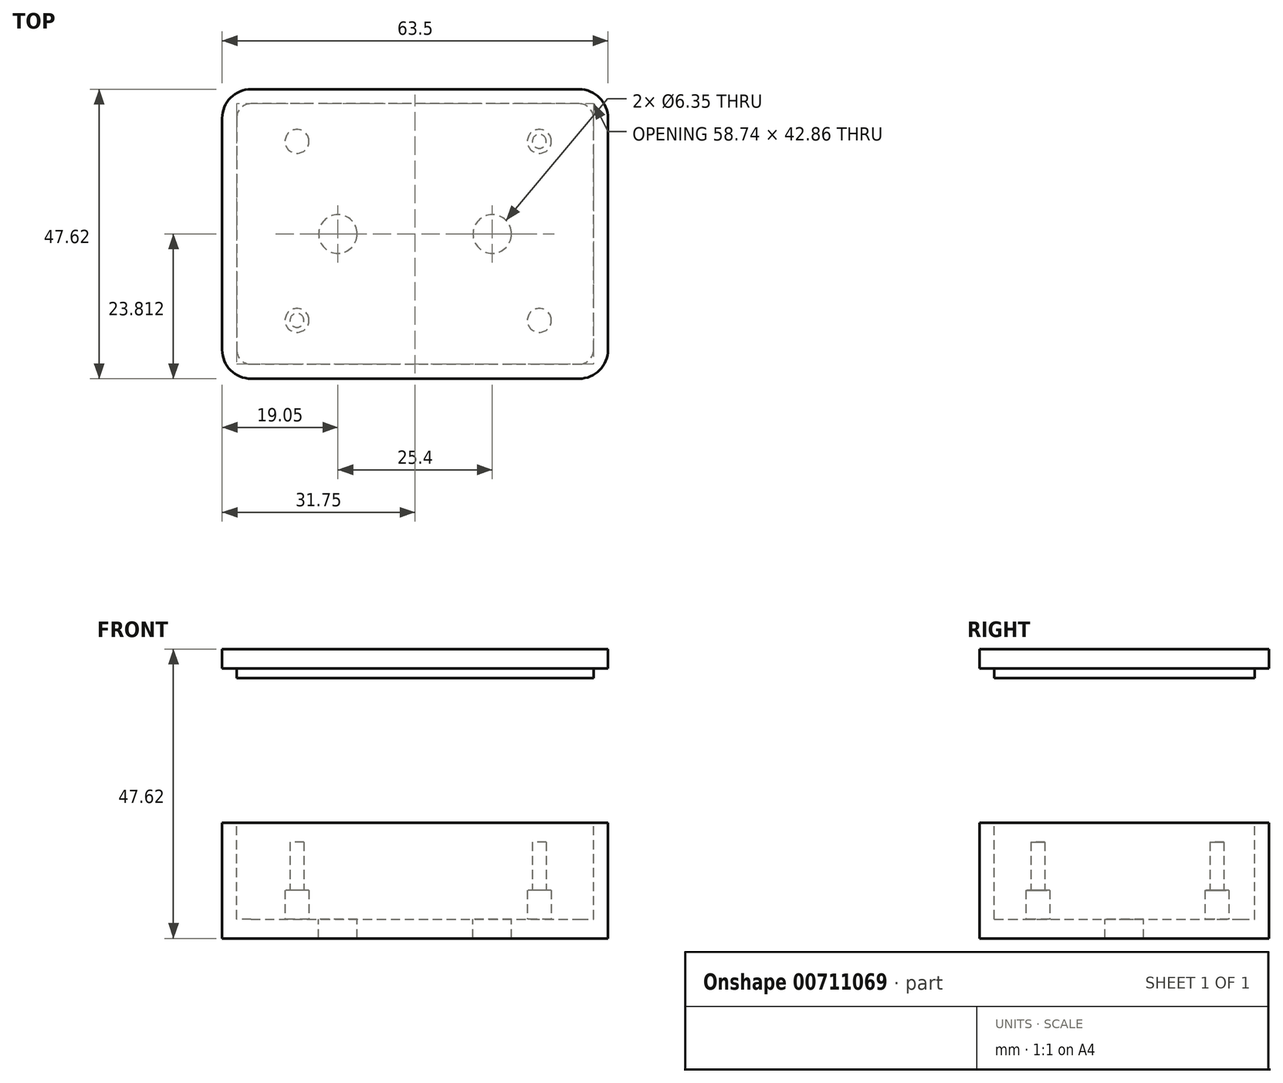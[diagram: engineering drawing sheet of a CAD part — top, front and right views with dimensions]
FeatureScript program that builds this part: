
annotation { "Feature Type Name" : "Feature", "Feature Type Description" : "" }
export const myFeature = defineFeature(function(context is Context, id is Id, definition is map)
    precondition{}
    {
        {
            var Q0;
            Q0=qCreatedBy(makeId("Top.planeOp"),FACE);
            var sketch = newSketch(context, id + "F0", { "sketchPlane" : qUnion([Q0])});
            skLineSegment(sketch, "E0.bottom", {"start": v(0, 0) * mm, "end": v(63.5, 0) * mm});
            skLineSegment(sketch, "E0.top", {"start": v(0, 47.62) * mm, "end": v(63.5, 47.62) * mm});
            skLineSegment(sketch, "E0.left", {"start": v(0, 0) * mm, "end": v(0, 47.62) * mm});
            skLineSegment(sketch, "E0.right", {"start": v(63.5, 0) * mm, "end": v(63.5, 47.62) * mm});
            skSolve(sketch);
        }
        {
            var Q0;
            Q0=makeQuery(id+"F0.imprint","IMPRINT",FACE,{"disambiguationData":[TD([[makeQuery(id+"F0.imprint","IMPRINT",EDGE,{"derivedFrom":sQuery(id+"F0.wireOp",EDGE,"E0.bottom")}),1.0]])]});
            extrude(context, id + "F1", {"entities" : qUnion([Q0]), "depth" : 19.05 * mm, "offsetDistance" : 25.4 * mm});
        }
        {
            var Q0;
            Q0=makeQuery(id+"F1.opExtrude","SWEPT_EDGE",EDGE,{"disambiguationData":[OSD([sQuery(id+"F0.wireOp",EDGE,"E0.bottom"),sQuery(id+"F0.wireOp",EDGE,"E0.left")])]});
            var Q1;
            Q1=makeQuery(id+"F1.opExtrude","SWEPT_EDGE",EDGE,{"disambiguationData":[OSD([sQuery(id+"F0.wireOp",EDGE,"E0.bottom"),sQuery(id+"F0.wireOp",EDGE,"E0.right")])]});
            var Q2;
            Q2=makeQuery(id+"F1.opExtrude","SWEPT_EDGE",EDGE,{"disambiguationData":[OSD([sQuery(id+"F0.wireOp",EDGE,"E0.top"),sQuery(id+"F0.wireOp",EDGE,"E0.right")])]});
            var Q3;
            Q3=makeQuery(id+"F1.opExtrude","SWEPT_EDGE",EDGE,{"disambiguationData":[OSD([sQuery(id+"F0.wireOp",EDGE,"E0.top"),sQuery(id+"F0.wireOp",EDGE,"E0.left")])]});
            fillet(context, id + "F2", {"entities" : qUnion([Q0, Q1, Q2, Q3]), "radius" : 4.76 * mm, "tangentPropagation" : true, "allowEdgeOverflow" : false});
        }
        {
            var Q0;
            Q0=makeQuery(id+"F1.opExtrude","CAP_FACE",FACE,{"disambiguationData":[OSD([sQuery(id+"F0.wireOp",EDGE,"E0.bottom"),sQuery(id+"F0.wireOp",EDGE,"E0.top"),sQuery(id+"F0.wireOp",EDGE,"E0.left"),sQuery(id+"F0.wireOp",EDGE,"E0.right")])],"isStart":false});
            var sketch = newSketch(context, id + "F3", { "sketchPlane" : qUnion([Q0])});
            skLineSegment(sketch, "E1.0", {"start": v(58.74, 45.24) * mm, "end": v(4.76, 45.24) * mm});
            skLineSegment(sketch, "E1.1", {"start": v(61.12, 4.76) * mm, "end": v(61.12, 42.86) * mm});
            skLineSegment(sketch, "E1.2", {"start": v(4.76, 2.38) * mm, "end": v(58.74, 2.38) * mm});
            skLineSegment(sketch, "E1.3", {"start": v(2.38, 42.86) * mm, "end": v(2.38, 4.76) * mm});
            skPoint(sketch, "E2.visualSharp", {"position": v(61.12, 45.24) * mm});
            skArc(sketch, "E2.filletArc", {"start": v(61.12, 42.86) * mm, "mid": v(60.42, 44.55) * mm, "end": v(58.74, 45.24) * mm});
            skPoint(sketch, "E3.visualSharp", {"position": v(61.12, 2.38) * mm});
            skArc(sketch, "E3.filletArc", {"start": v(58.74, 2.38) * mm, "mid": v(60.42, 3.08) * mm, "end": v(61.12, 4.76) * mm});
            skPoint(sketch, "E4.visualSharp", {"position": v(2.38, 2.38) * mm});
            skArc(sketch, "E4.filletArc", {"start": v(2.38, 4.76) * mm, "mid": v(3.08, 3.08) * mm, "end": v(4.76, 2.38) * mm});
            skPoint(sketch, "E5.visualSharp", {"position": v(2.38, 45.24) * mm});
            skArc(sketch, "E5.filletArc", {"start": v(4.76, 45.24) * mm, "mid": v(3.08, 44.55) * mm, "end": v(2.38, 42.86) * mm});
            skSolve(sketch);
        }
        {
            var Q0;
            Q0 = qSketchRegion(id + "F3", true);
            var Q1;
            Q1=sQuery(id+"F3.wireOp",EDGE,"E1.1");
            extrude(context, id + "F4", {"entities" : qUnion([Q0]), "operationType" : NewBodyOperationType.REMOVE, "surfaceEntities" : qUnion([Q1]), "oppositeDirection" : true, "depth" : 15.88 * mm, "offsetDistance" : 25.4 * mm});
        }
        {
            var Q0;
            Q0=makeQuery(id+"F4.boolean.opBoolean","COPY",FACE,{"derivedFrom":makeQuery(id+"F4.opExtrude","CAP_FACE",FACE,{"disambiguationData":[OSD([sQuery(id+"F3.wireOp",EDGE,"E1.0"),sQuery(id+"F3.wireOp",EDGE,"E1.1"),sQuery(id+"F3.wireOp",EDGE,"E1.2"),sQuery(id+"F3.wireOp",EDGE,"E1.3"),sQuery(id+"F3.wireOp",EDGE,"E2.filletArc"),sQuery(id+"F3.wireOp",EDGE,"E3.filletArc"),sQuery(id+"F3.wireOp",EDGE,"E4.filletArc"),sQuery(id+"F3.wireOp",EDGE,"E5.filletArc")])],"isStart":false})});
            var sketch = newSketch(context, id + "F5", { "sketchPlane" : qUnion([Q0])});
            skCircle(sketch, "E6", {"center": v(12.32, 9.59) * mm, "radius": 1.14 * mm});
            skCircle(sketch, "E7", {"center": v(52.2, 39.05) * mm, "radius": 1.14 * mm});
            skLineSegment(sketch, "E8.bottom", {"start": v(55.25, 42.1) * mm, "end": v(8.25, 42.1) * mm, "construction": true});
            skLineSegment(sketch, "E8.top", {"start": v(55.25, 5.52) * mm, "end": v(8.25, 5.52) * mm, "construction": true});
            skLineSegment(sketch, "E8.left", {"start": v(55.25, 42.1) * mm, "end": v(55.25, 5.52) * mm, "construction": true});
            skLineSegment(sketch, "E8.right", {"start": v(8.25, 42.1) * mm, "end": v(8.25, 5.52) * mm, "construction": true});
            skLineSegment(sketch, "E9", {"start": v(31.75, 5.52) * mm, "end": v(31.75, 2.38) * mm, "construction": true});
            skLineSegment(sketch, "E10", {"start": v(55.25, 23.81) * mm, "end": v(61.12, 23.81) * mm, "construction": true});
            skSolve(sketch);
        }
        {
            var Q0;
            Q0 = qSketchRegion(id + "F5", true);
            var Q1;
            Q1=sQuery(id+"F5.wireOp",EDGE,"E6");
            var Q2;
            Q2=makeQuery(id+"F1.opExtrude","CAP_FACE",FACE,{"disambiguationData":[OSD([sQuery(id+"F0.wireOp",EDGE,"E0.bottom"),sQuery(id+"F0.wireOp",EDGE,"E0.top"),sQuery(id+"F0.wireOp",EDGE,"E0.left"),sQuery(id+"F0.wireOp",EDGE,"E0.right")])],"isStart":false});
            extrude(context, id + "F6", {"entities" : qUnion([Q0]), "operationType" : NewBodyOperationType.ADD, "surfaceEntities" : qUnion([Q1]), "depth" : 12.7 * mm, "endBoundEntityFace" : qUnion([Q2]), "offsetDistance" : 25.4 * mm});
        }
        {
            var Q0;
            Q0=makeQuery(id+"F4.boolean.opBoolean","COPY",FACE,{"derivedFrom":makeQuery(id+"F4.opExtrude","CAP_FACE",FACE,{"disambiguationData":[OSD([sQuery(id+"F3.wireOp",EDGE,"E1.0"),sQuery(id+"F3.wireOp",EDGE,"E1.1"),sQuery(id+"F3.wireOp",EDGE,"E1.2"),sQuery(id+"F3.wireOp",EDGE,"E1.3"),sQuery(id+"F3.wireOp",EDGE,"E2.filletArc"),sQuery(id+"F3.wireOp",EDGE,"E3.filletArc"),sQuery(id+"F3.wireOp",EDGE,"E4.filletArc"),sQuery(id+"F3.wireOp",EDGE,"E5.filletArc")])],"isStart":false})});
            var sketch = newSketch(context, id + "F7", { "sketchPlane" : qUnion([Q0])});
            skCircle(sketch, "E11.0", {"center": v(12.32, 9.59) * mm, "radius": 1.97 * mm});
            skCircle(sketch, "E12.0", {"center": v(52.2, 39.05) * mm, "radius": 1.97 * mm});
            skCircle(sketch, "E13", {"center": v(12.32, 39.05) * mm, "radius": 1.97 * mm});
            skCircle(sketch, "E14", {"center": v(52.2, 9.59) * mm, "radius": 1.97 * mm});
            skSolve(sketch);
        }
        {
            var Q0;
            Q0 = qSketchRegion(id + "F7", true);
            extrude(context, id + "F8", {"entities" : qUnion([Q0]), "operationType" : NewBodyOperationType.ADD, "depth" : 4.76 * mm, "offsetDistance" : 25.4 * mm});
        }
        {
            var Q0;
            Q0=makeQuery(id+"F4.boolean.opBoolean","COPY",FACE,{"derivedFrom":makeQuery(id+"F4.opExtrude","CAP_FACE",FACE,{"disambiguationData":[OSD([sQuery(id+"F3.wireOp",EDGE,"E1.0"),sQuery(id+"F3.wireOp",EDGE,"E1.1"),sQuery(id+"F3.wireOp",EDGE,"E1.2"),sQuery(id+"F3.wireOp",EDGE,"E1.3"),sQuery(id+"F3.wireOp",EDGE,"E2.filletArc"),sQuery(id+"F3.wireOp",EDGE,"E3.filletArc"),sQuery(id+"F3.wireOp",EDGE,"E4.filletArc"),sQuery(id+"F3.wireOp",EDGE,"E5.filletArc")])],"isStart":false})});
            var sketch = newSketch(context, id + "F9", { "sketchPlane" : qUnion([Q0])});
            skCircle(sketch, "E15", {"center": v(44.45, 23.81) * mm, "radius": 3.18 * mm});
            skCircle(sketch, "E16", {"center": v(19.05, 23.81) * mm, "radius": 3.18 * mm});
            skLineSegment(sketch, "E17", {"start": v(44.45, 23.81) * mm, "end": v(19.05, 23.81) * mm, "construction": true});
            skLineSegment(sketch, "E18", {"start": v(31.75, 23.81) * mm, "end": v(31.75, 2.38) * mm, "construction": true});
            skLineSegment(sketch, "E19", {"start": v(31.75, 23.81) * mm, "end": v(31.75, 45.24) * mm, "construction": true});
            skSolve(sketch);
        }
        {
            var Q0;
            Q0 = qSketchRegion(id + "F9", true);
            extrude(context, id + "F10", {"entities" : qUnion([Q0]), "operationType" : NewBodyOperationType.REMOVE, "oppositeDirection" : true, "depth" : 25.4 * mm, "offsetDistance" : 25.4 * mm});
        }
        {
            var Q0;
            Q0=makeQuery(id+"F1.opExtrude","CAP_FACE",FACE,{"disambiguationData":[OSD([sQuery(id+"F0.wireOp",EDGE,"E0.bottom"),sQuery(id+"F0.wireOp",EDGE,"E0.top"),sQuery(id+"F0.wireOp",EDGE,"E0.left"),sQuery(id+"F0.wireOp",EDGE,"E0.right")])],"isStart":false});
            cPlane(context, id + "F11", {"entities" : qUnion([Q0]), "cplaneType" : CPlaneType.OFFSET, "offset" : 25.4 * mm, "width" : 152.4 * mm, "height" : 152.4 * mm});
        }
        {
            var Q0;
            Q0=qCreatedBy(id+"F11.planeOp",FACE);
            var sketch = newSketch(context, id + "F12", { "sketchPlane" : qUnion([Q0])});
            skLineSegment(sketch, "E20.0", {"start": v(0, 4.76) * mm, "end": v(0, 42.86) * mm});
            skLineSegment(sketch, "E21.0", {"start": v(4.76, 47.62) * mm, "end": v(58.74, 47.62) * mm});
            skArc(sketch, "E22.0", {"start": v(4.76, 47.62) * mm, "mid": v(1.4, 46.23) * mm, "end": v(0, 42.86) * mm});
            skArc(sketch, "E23.0", {"start": v(63.5, 42.86) * mm, "mid": v(62.1, 46.23) * mm, "end": v(58.74, 47.62) * mm});
            skLineSegment(sketch, "E24.0", {"start": v(63.5, 4.76) * mm, "end": v(63.5, 42.86) * mm});
            skArc(sketch, "E25.0", {"start": v(58.74, 0) * mm, "mid": v(62.1, 1.4) * mm, "end": v(63.5, 4.76) * mm});
            skLineSegment(sketch, "E26.0", {"start": v(4.76, 0) * mm, "end": v(58.74, 0) * mm});
            skArc(sketch, "E27.0", {"start": v(0, 4.76) * mm, "mid": v(1.4, 1.4) * mm, "end": v(4.76, 0) * mm});
            skSolve(sketch);
        }
        {
            var Q0;
            Q0=makeQuery(id+"F12.imprint","IMPRINT",FACE,{"disambiguationData":[TD([[makeQuery(id+"F12.imprint","IMPRINT",EDGE,{"derivedFrom":sQuery(id+"F12.wireOp",EDGE,"E20.0")}),-1.0]])]});
            var Q1;
            Q1=sQuery(id+"F12.wireOp",EDGE,"E20.0");
            extrude(context, id + "F13", {"entities" : qUnion([Q0]), "surfaceEntities" : qUnion([Q1]), "depth" : 3.17 * mm, "offsetDistance" : 25.4 * mm});
        }
        {
            var Q0;
            Q0=makeQuery(id+"F13.opExtrude","CAP_FACE",FACE,{"disambiguationData":[OSD([sQuery(id+"F12.wireOp",EDGE,"E20.0"),sQuery(id+"F12.wireOp",EDGE,"E21.0"),sQuery(id+"F12.wireOp",EDGE,"E22.0"),sQuery(id+"F12.wireOp",EDGE,"E23.0"),sQuery(id+"F12.wireOp",EDGE,"E24.0"),sQuery(id+"F12.wireOp",EDGE,"E25.0"),sQuery(id+"F12.wireOp",EDGE,"E26.0"),sQuery(id+"F12.wireOp",EDGE,"E27.0")])],"isStart":true});
            var sketch = newSketch(context, id + "F14", { "sketchPlane" : qUnion([Q0])});
            skLineSegment(sketch, "E28.0", {"start": v(58.74, -45.24) * mm, "end": v(4.76, -45.24) * mm});
            skLineSegment(sketch, "E28.1", {"start": v(61.12, -4.76) * mm, "end": v(61.12, -42.86) * mm});
            skLineSegment(sketch, "E28.2", {"start": v(4.76, -2.38) * mm, "end": v(58.74, -2.38) * mm});
            skLineSegment(sketch, "E28.3", {"start": v(2.38, -42.86) * mm, "end": v(2.38, -4.76) * mm});
            skPoint(sketch, "E28.4", {"position": v(61.12, -45.24) * mm});
            skArc(sketch, "E28.5", {"start": v(61.12, -42.86) * mm, "mid": v(60.42, -44.55) * mm, "end": v(58.74, -45.24) * mm});
            skPoint(sketch, "E28.6", {"position": v(61.12, -2.38) * mm});
            skArc(sketch, "E28.7", {"start": v(58.74, -2.38) * mm, "mid": v(60.42, -3.08) * mm, "end": v(61.12, -4.76) * mm});
            skPoint(sketch, "E28.8", {"position": v(2.38, -2.38) * mm});
            skArc(sketch, "E28.9", {"start": v(2.38, -4.76) * mm, "mid": v(3.08, -3.08) * mm, "end": v(4.76, -2.38) * mm});
            skPoint(sketch, "E28.10", {"position": v(2.38, -45.24) * mm});
            skArc(sketch, "E28.11", {"start": v(4.76, -45.24) * mm, "mid": v(3.08, -44.55) * mm, "end": v(2.38, -42.86) * mm});
            skSolve(sketch);
        }
        {
            var Q0;
            Q0=makeQuery(id+"F14.imprint","IMPRINT",FACE,{"disambiguationData":[TD([[makeQuery(id+"F14.imprint","IMPRINT",EDGE,{"derivedFrom":sQuery(id+"F14.wireOp",EDGE,"E28.0")}),-1.0]])]});
            extrude(context, id + "F15", {"entities" : qUnion([Q0]), "operationType" : NewBodyOperationType.ADD, "depth" : 1.59 * mm, "offsetDistance" : 25.4 * mm});
        }
    });
